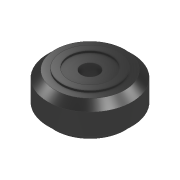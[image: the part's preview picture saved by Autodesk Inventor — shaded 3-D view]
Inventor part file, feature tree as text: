
AUTODESK INVENTOR PART (.ipt)
format: ipt  version: 2020 (Build 240168000, 168)  size: 137,728 bytes
history: native  units: mm
features: mirror x1
ambient origin geometry x8: Origin, YZ Plane, XZ Plane, XY Plane, X Axis, Y Axis, Z Axis, Center Point
bodies: Solid1 (feature_tree)
feature tree (1):
  mirror  "Mirror1"
